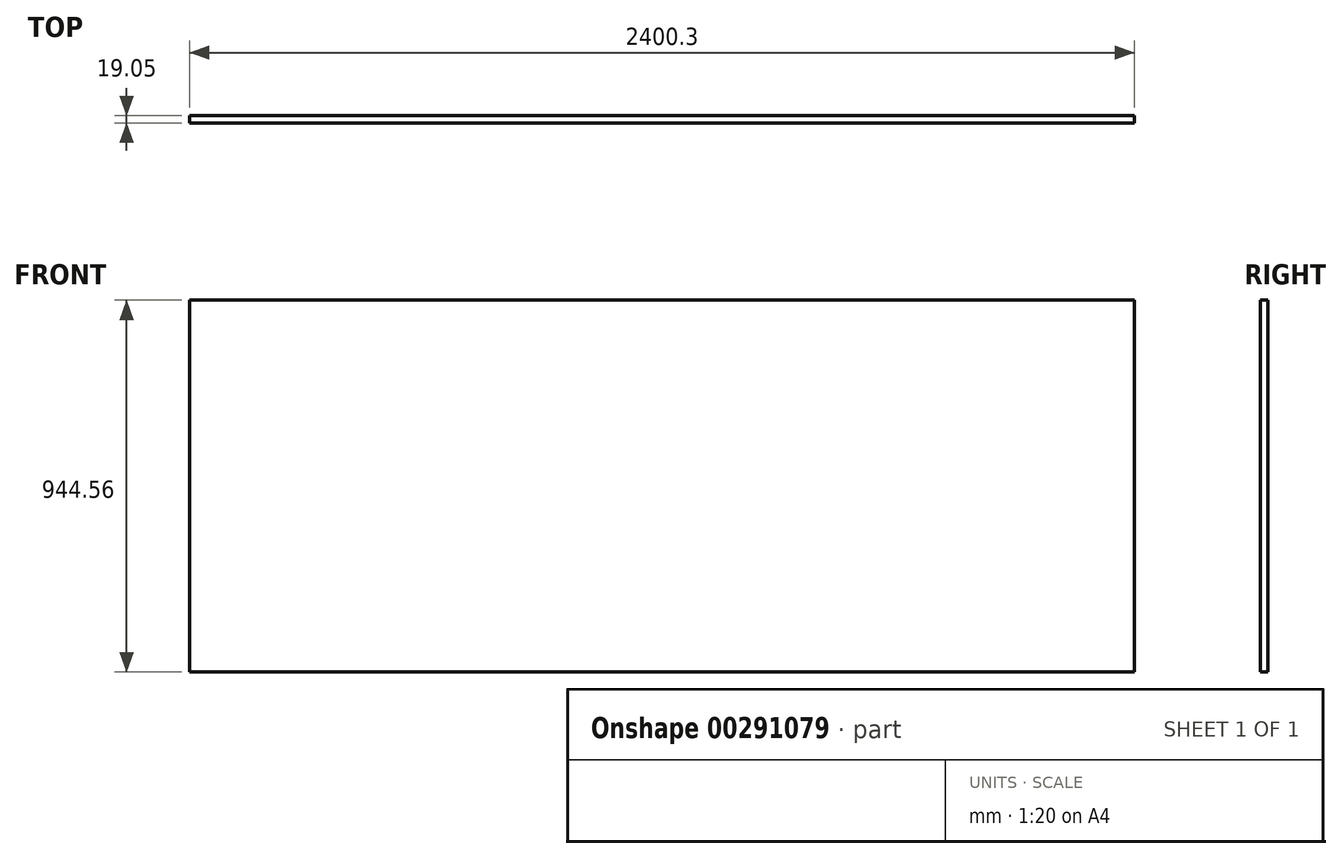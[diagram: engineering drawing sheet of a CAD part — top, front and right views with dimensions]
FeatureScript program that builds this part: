
annotation { "Feature Type Name" : "Feature", "Feature Type Description" : "" }
export const myFeature = defineFeature(function(context is Context, id is Id, definition is map)
    precondition{}
    {
        {
            var Q0;
            Q0=qCreatedBy(makeId("Front.planeOp"),FACE);
            var sketch = newSketch(context, id + "F0", { "sketchPlane" : qUnion([Q0])});
            skLineSegment(sketch, "E0.bottom", {"start": v(0, 0) * mm, "end": v(2400.3, 0) * mm});
            skLineSegment(sketch, "E0.top", {"start": v(0, -944.56) * mm, "end": v(2400.3, -944.56) * mm});
            skLineSegment(sketch, "E0.left", {"start": v(0, 0) * mm, "end": v(0, -944.56) * mm});
            skLineSegment(sketch, "E0.right", {"start": v(2400.3, 0) * mm, "end": v(2400.3, -944.56) * mm});
            skSolve(sketch);
        }
        {
            var Q0;
            Q0 = qSketchRegion(id + "F0", true);
            extrude(context, id + "F1", {"entities" : qUnion([Q0]), "depth" : 19.05 * mm});
        }
    });
